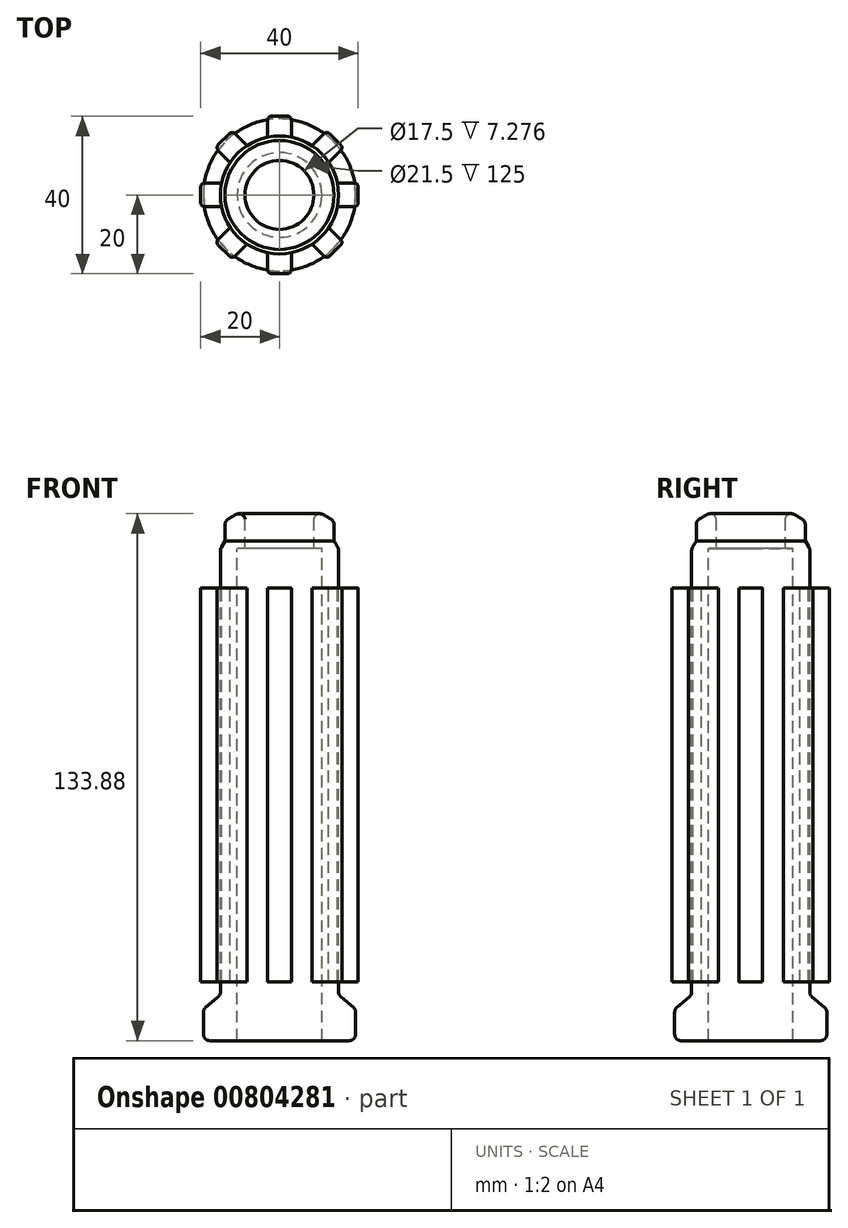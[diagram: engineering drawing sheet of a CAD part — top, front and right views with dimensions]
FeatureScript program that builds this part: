
annotation { "Feature Type Name" : "Feature", "Feature Type Description" : "" }
export const myFeature = defineFeature(function(context is Context, id is Id, definition is map)
    precondition{}
    {
        {
            var Q0;
            Q0=qCreatedBy(makeId("Front.planeOp"),FACE);
            var sketch = newSketch(context, id + "F0", { "sketchPlane" : qUnion([Q0])});
            skLineSegment(sketch, "E0", {"start": v(0, 31.56) * mm, "end": v(0, 0) * mm, "construction": true});
            skLineSegment(sketch, "E1", {"start": v(8.75, 135) * mm, "end": v(8.75, 125) * mm});
            skLineSegment(sketch, "E2", {"start": v(8.75, 125) * mm, "end": v(10.75, 125) * mm});
            skLineSegment(sketch, "E3", {"start": v(10.75, 125) * mm, "end": v(10.75, 0) * mm});
            skLineSegment(sketch, "E4", {"start": v(10.75, 0) * mm, "end": v(19.33, 0) * mm});
            skLineSegment(sketch, "E5", {"start": v(19.33, 0) * mm, "end": v(19.33, 8) * mm});
            skLineSegment(sketch, "E6", {"start": v(19.33, 8) * mm, "end": v(15, 11.63) * mm});
            skLineSegment(sketch, "E7", {"start": v(15, 11.63) * mm, "end": v(15, 125) * mm});
            skLineSegment(sketch, "E8", {"start": v(15, 125) * mm, "end": v(13.85, 127) * mm});
            skLineSegment(sketch, "E9", {"start": v(13.85, 127) * mm, "end": v(13.85, 132) * mm});
            skArc(sketch, "E10", {"start": v(13.85, 132) * mm, "mid": v(11.33, 133.56) * mm, "end": v(8.75, 135) * mm});
            skSolve(sketch);
        }
        {
            var Q0;
            Q0=makeQuery(id+"F0.imprint","IMPRINT",FACE,{"disambiguationData":[TD([[makeQuery(id+"F0.imprint","IMPRINT",EDGE,{"derivedFrom":sQuery(id+"F0.wireOp",EDGE,"E1")}),1.0]])]});
            var Q1;
            Q1=sQuery(id+"F0.wireOp",EDGE,"E0");
            revolve(context, id + "F1", {"surfaceOperationType" : NewSurfaceOperationType.NEW, "entities" : qUnion([Q0]), "axis" : qUnion([Q1]), "revolveType" : RevolveType.FULL});
        }
        {
            var Q0;
            Q0=makeQuery(id+"F1.opRevolve","SWEPT_EDGE",EDGE,{"disambiguationData":[OSD([sQuery(id+"F0.wireOp",EDGE,"E1"),sQuery(id+"F0.wireOp",EDGE,"E10")])]});
            var Q1;
            Q1=makeQuery(id+"F1.opRevolve","SWEPT_EDGE",EDGE,{"disambiguationData":[OSD([sQuery(id+"F0.wireOp",EDGE,"E9"),sQuery(id+"F0.wireOp",EDGE,"E10")])]});
            var Q2;
            Q2=makeQuery(id+"F1.opRevolve","SWEPT_EDGE",EDGE,{"disambiguationData":[OSD([sQuery(id+"F0.wireOp",EDGE,"E7"),sQuery(id+"F0.wireOp",EDGE,"E8")])]});
            var Q3;
            Q3=makeQuery(id+"F1.opRevolve","SWEPT_EDGE",EDGE,{"disambiguationData":[OSD([sQuery(id+"F0.wireOp",EDGE,"E6"),sQuery(id+"F0.wireOp",EDGE,"E7")])]});
            var Q4;
            Q4=makeQuery(id+"F1.opRevolve","SWEPT_EDGE",EDGE,{"disambiguationData":[OSD([sQuery(id+"F0.wireOp",EDGE,"E5"),sQuery(id+"F0.wireOp",EDGE,"E6")])]});
            var Q5;
            Q5=makeQuery(id+"F1.opRevolve","SWEPT_EDGE",EDGE,{"disambiguationData":[OSD([sQuery(id+"F0.wireOp",EDGE,"E4"),sQuery(id+"F0.wireOp",EDGE,"E5")])]});
            fillet(context, id + "F2", {"entities" : qUnion([Q0, Q1, Q2, Q3, Q4, Q5]), "radius" : 1.6 * mm, "tangentPropagation" : true, "allowEdgeOverflow" : false});
        }
        {
            var Q0;
            Q0=qCreatedBy(makeId("Right.planeOp"),FACE);
            cPlane(context, id + "F3", {"entities" : qUnion([Q0]), "cplaneType" : CPlaneType.OFFSET, "offset" : 20 * mm, "width" : 150 * mm, "height" : 150 * mm});
        }
        {
            var Q0;
            Q0=qCreatedBy(id+"F3.planeOp",FACE);
            var sketch = newSketch(context, id + "F4", { "sketchPlane" : qUnion([Q0])});
            skLineSegment(sketch, "E11.bottom", {"start": v(-3, 115) * mm, "end": v(3, 115) * mm});
            skLineSegment(sketch, "E11.top", {"start": v(-3, 15) * mm, "end": v(3, 15) * mm});
            skLineSegment(sketch, "E11.left", {"start": v(-3, 115) * mm, "end": v(-3, 15) * mm});
            skLineSegment(sketch, "E11.right", {"start": v(3, 115) * mm, "end": v(3, 15) * mm});
            skSolve(sketch);
        }
        {
            var Q0;
            Q0=makeQuery(id+"F4.imprint","IMPRINT",FACE,{"disambiguationData":[TD([[makeQuery(id+"F4.imprint","IMPRINT",EDGE,{"derivedFrom":sQuery(id+"F4.wireOp",EDGE,"E11.bottom")}),-1.0]])]});
            var Q1;
            Q1=makeQuery(id+"F1.opRevolve","SWEPT_FACE",FACE,{"disambiguationData":[OSD([sQuery(id+"F0.wireOp",EDGE,"E7")])]});
            extrude(context, id + "F5", {"entities" : qUnion([Q0]), "endBound" : BoundingType.UP_TO_SURFACE, "oppositeDirection" : true, "depth" : 25 * mm, "endBoundEntityFace" : qUnion([Q1]), "offsetDistance" : 25 * mm});
        }
        {
            var Q0;
            Q0=makeQuery(id+"F5.opExtrude","CAP_EDGE",EDGE,{"disambiguationData":[OSD([sQuery(id+"F4.wireOp",EDGE,"E11.left")])],"isStart":true});
            var Q1;
            Q1=makeQuery(id+"F5.opExtrude","CAP_EDGE",EDGE,{"disambiguationData":[OSD([sQuery(id+"F4.wireOp",EDGE,"E11.right")])],"isStart":true});
            fillet(context, id + "F6", {"entities" : qUnion([Q0, Q1]), "radius" : 1 * mm, "tangentPropagation" : true, "allowEdgeOverflow" : false});
        }
        {
            var Q0;
            Q0=makeQuery(id+"F5.opExtrude","SWEPT_BODY",BODY,{"disambiguationData":[OSD([sQuery(id+"F4.wireOp",EDGE,"E11.bottom"),sQuery(id+"F4.wireOp",EDGE,"E11.top"),sQuery(id+"F4.wireOp",EDGE,"E11.left"),sQuery(id+"F4.wireOp",EDGE,"E11.right")])]});
            var Q1;
            {var subQ0=sQuery(id+"F0.wireOp",EDGE,"E7");Q1=makeQuery(id+"F2.opFillet","BLEND_EDGE",EDGE,{"blendedFrom":[makeQuery(id+"F1.opRevolve","SWEPT_EDGE",EDGE,{"disambiguationData":[OSD([sQuery(id+"F0.wireOp",EDGE,"E6"),subQ0])]}),makeQuery(id+"F1.opRevolve","SWEPT_FACE",FACE,{"disambiguationData":[OSD([subQ0])]})],"blendedInto":[makeQuery(id+"F1.opRevolve","SWEPT_FACE",FACE,{"disambiguationData":[OSD([subQ0])]})]});}
            circularPattern(context, id + "F7", {"entities" : qUnion([Q0]), "axis" : qUnion([Q1]), "angle" : 360 * degree, "instanceCount" : 8, "equalSpace" : true});
        }
    });
